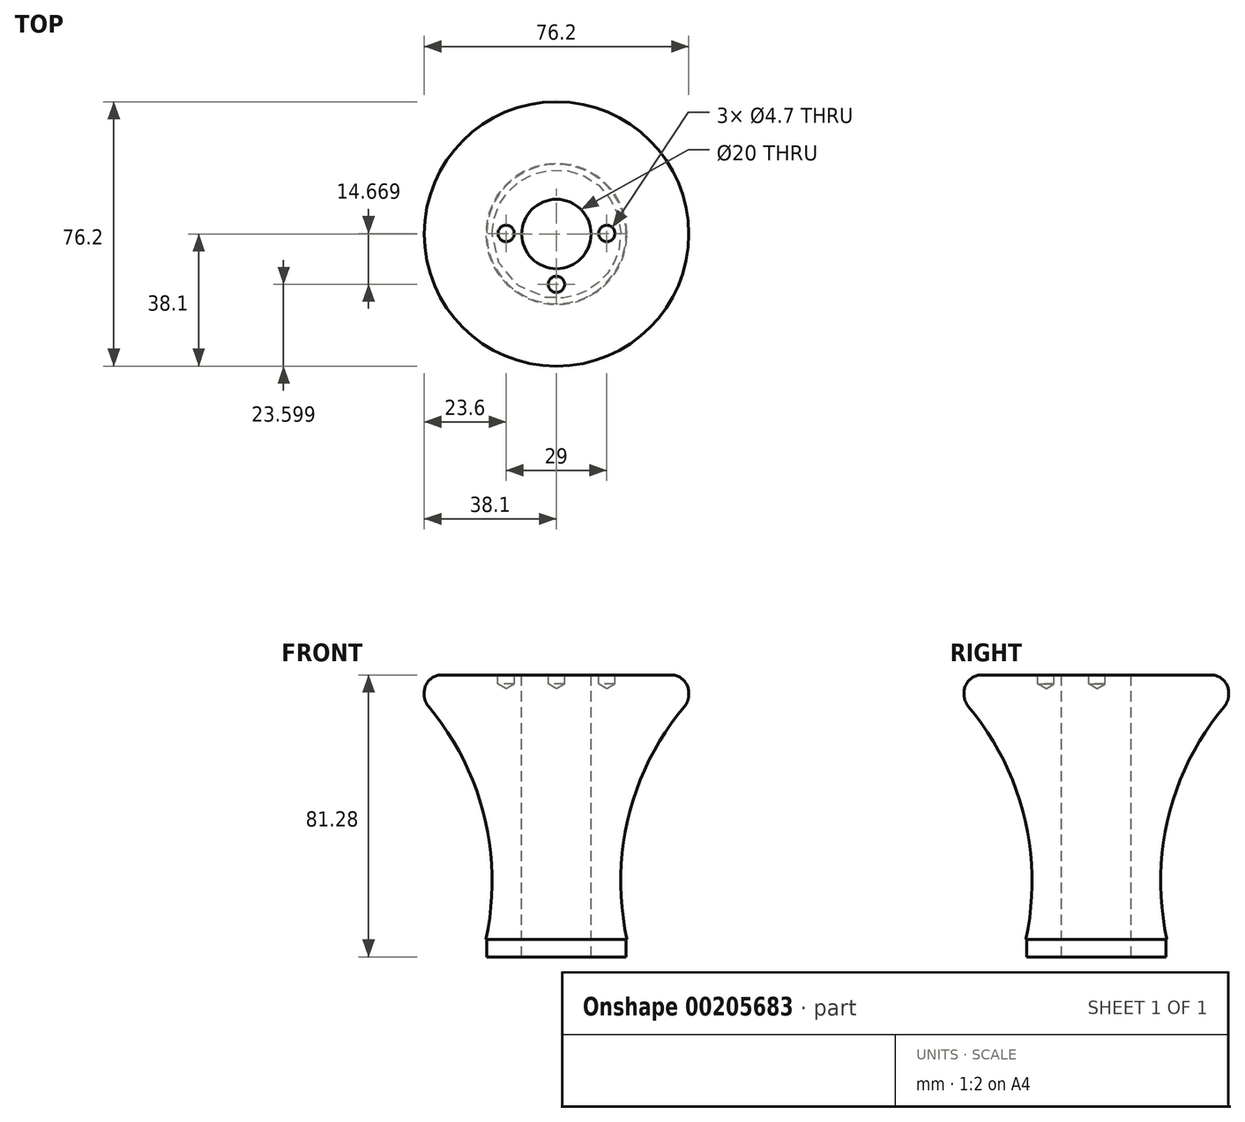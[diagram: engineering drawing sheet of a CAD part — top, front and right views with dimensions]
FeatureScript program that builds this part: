
annotation { "Feature Type Name" : "Feature", "Feature Type Description" : "" }
export const myFeature = defineFeature(function(context is Context, id is Id, definition is map)
    precondition{}
    {
        {
            var Q0;
            Q0=qCreatedBy(makeId("Right.planeOp"),FACE);
            var sketch = newSketch(context, id + "F0", { "sketchPlane" : qUnion([Q0])});
            skLineSegment(sketch, "E0", {"start": v(0, 0) * mm, "end": v(-20.32, 0) * mm});
            skLineSegment(sketch, "E1", {"start": v(-20.32, 0) * mm, "end": v(-10.16, 0) * mm});
            skLineSegment(sketch, "E2", {"start": v(-38.1, 68.58) * mm, "end": v(0, 68.58) * mm});
            skLineSegment(sketch, "E3", {"start": v(0, 68.58) * mm, "end": v(0, 0) * mm});
            skArc(sketch, "E4", {"start": v(-20.32, 0) * mm, "mid": v(-21.05, 36.4) * mm, "end": v(-38.1, 68.58) * mm});
            skSolve(sketch);
        }
        {
            var Q0;
            Q0=qCreatedBy(makeId("Right.planeOp"),FACE);
            var sketch = newSketch(context, id + "F1", { "sketchPlane" : qUnion([Q0])});
            skLineSegment(sketch, "E5", {"start": v(0, 0) * mm, "end": v(0, 42.89) * mm});
            skSolve(sketch);
        }
        {
            var Q0;
            Q0=makeQuery(id+"F0.imprint","IMPRINT",FACE,{"disambiguationData":[TD([[makeQuery(id+"F0.imprint","IMPRINT",EDGE,{"derivedFrom":sQuery(id+"F0.wireOp",EDGE,"E0")}),-1.0]])]});
            var Q1;
            Q1=sQuery(id+"F1.wireOp",EDGE,"E5");
            revolve(context, id + "F2", {"entities" : qUnion([Q0]), "axis" : qUnion([Q1]), "revolveType" : RevolveType.FULL});
        }
        {
            var Q0;
            Q0=qCreatedBy(makeId("Top.planeOp"),FACE);
            var sketch = newSketch(context, id + "F3", { "sketchPlane" : qUnion([Q0])});
            skCircle(sketch, "E6", {"center": v(0, 0) * mm, "radius": 20.1 * mm});
            skSolve(sketch);
        }
        {
            var Q0;
            Q0=makeQuery(id+"F3.imprint","IMPRINT",FACE,{"disambiguationData":[TD([[makeQuery(id+"F3.imprint","IMPRINT",EDGE,{"derivedFrom":sQuery(id+"F3.wireOp",EDGE,"E6")}),1.0]])]});
            extrude(context, id + "F4", {"entities" : qUnion([Q0]), "operationType" : NewBodyOperationType.ADD, "oppositeDirection" : true, "depth" : 5.08 * mm});
        }
        {
            var Q0;
            Q0=makeQuery(id+"F2.opRevolve","SWEPT_FACE",FACE,{"disambiguationData":[OSD([sQuery(id+"F0.wireOp",EDGE,"E2")])]});
            extrude(context, id + "F5", {"entities" : qUnion([Q0]), "operationType" : NewBodyOperationType.ADD, "depth" : 7.62 * mm});
        }
        {
            var Q0;
            Q0=makeQuery(id+"F5.opExtrude","CAP_EDGE",EDGE,{"disambiguationData":[OSD([sQuery(id+"F0.wireOp",EDGE,"E2"),sQuery(id+"F0.wireOp",EDGE,"E4")])],"isStart":false});
            var Q1;
            {var subQ0=sQuery(id+"F0.wireOp",EDGE,"E4");var subQ1=sQuery(id+"F0.wireOp",EDGE,"E2");Q1=makeQuery(id+"F5.boolean.opBoolean","MERGE",EDGE,{"derivedFrom":[makeQuery(id+"F2.opRevolve","SWEPT_EDGE",EDGE,{"disambiguationData":[OSD([subQ1,subQ0])]}),makeQuery(id+"F5.opExtrude","CAP_EDGE",EDGE,{"disambiguationData":[OSD([subQ1,subQ0])],"isStart":true})]});}
            fillet(context, id + "F6", {"entities" : qUnion([Q0, Q1]), "radius" : 5.08 * mm, "tangentPropagation" : true, "allowEdgeOverflow" : false});
        }
        {
            var Q0;
            Q0=makeQuery(id+"F5.opExtrude","CAP_FACE",FACE,{"disambiguationData":[OSD([sQuery(id+"F0.wireOp",EDGE,"E2")])],"isStart":false});
            var sketch = newSketch(context, id + "F7", { "sketchPlane" : qUnion([Q0])});
            skCircle(sketch, "E7", {"center": v(0, 0) * mm, "radius": 14.5 * mm});
            skPoint(sketch, "E8", {"position": v(0, -14.5) * mm});
            skPoint(sketch, "E9", {"position": v(-14.5, 0.17) * mm});
            skPoint(sketch, "E10", {"position": v(14.5, 0.17) * mm});
            skSolve(sketch);
        }
        {
            var Q0;
            Q0=sQuery(id+"F7.wireOp",VERTEX,"E10");
            var Q1;
            Q1=sQuery(id+"F7.wireOp",VERTEX,"E9");
            var Q2;
            Q2=sQuery(id+"F7.wireOp",VERTEX,"E8");
            var Q3;
            Q3=makeQuery(id+"F2.opRevolve","SWEPT_BODY",BODY,{"disambiguationData":[OSD([sQuery(id+"F0.wireOp",EDGE,"E0"),sQuery(id+"F0.wireOp",EDGE,"E1"),sQuery(id+"F0.wireOp",EDGE,"E2"),sQuery(id+"F0.wireOp",EDGE,"E3"),sQuery(id+"F0.wireOp",EDGE,"E4")])]});
            hole(context, id + "F8", {"style" : HoleStyle.SIMPLE, "endStyle" : HoleEndStyle.BLIND, "holeDiameter" : 4.7 * mm, "holeDepth" : 2.54 * mm, "startFromSketch" : true, "locations" : qUnion([Q0, Q1, Q2]), "scope" : qUnion([Q3])});
        }
        {
            var Q0;
            Q0=makeQuery(id+"F5.opExtrude","CAP_FACE",FACE,{"disambiguationData":[OSD([sQuery(id+"F0.wireOp",EDGE,"E2")])],"isStart":false});
            var sketch = newSketch(context, id + "F9", { "sketchPlane" : qUnion([Q0])});
            skCircle(sketch, "E11", {"center": v(0, 0) * mm, "radius": 10 * mm});
            skSolve(sketch);
        }
        {
            var Q0;
            Q0=makeQuery(id+"F9.imprint","IMPRINT",FACE,{"disambiguationData":[TD([[makeQuery(id+"F9.imprint","IMPRINT",EDGE,{"derivedFrom":sQuery(id+"F9.wireOp",EDGE,"E11")}),1.0]])]});
            var Q1;
            Q1=sQuery(id+"F9.wireOp",EDGE,"E11");
            extrude(context, id + "F10", {"entities" : qUnion([Q0]), "operationType" : NewBodyOperationType.REMOVE, "surfaceEntities" : qUnion([Q1]), "endBound" : BoundingType.THROUGH_ALL, "oppositeDirection" : true, "depth" : 50 * mm});
        }
    });
